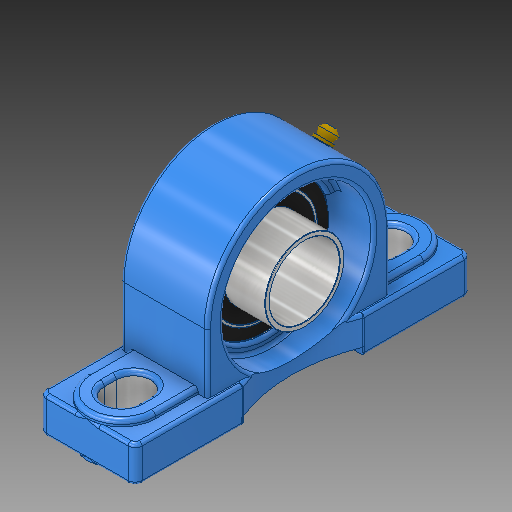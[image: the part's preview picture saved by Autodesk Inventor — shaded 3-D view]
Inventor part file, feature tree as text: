
AUTODESK INVENTOR PART (.ipt)
format: ipt  version: 2019 (Build 230136000, 136)  size: 796,672 bytes
history: native  units: mm
features: sketch x28, extrude x23, fillet x14, plane x8, mirror x6, revolve x1
ambient origin geometry x8: Origin, YZ Plane, XZ Plane, XY Plane, X Axis, Y Axis, Z Axis, Center Point
bodies: Solid1 (feature_tree)
feature tree (80):
  extrude  "Extrusion1"  Depth=167.0mm
  fillet  "Fillet1"  Radius=23.8mm
  plane  "Work Plane1"
  extrude  "Extrusion2"  Depth=18.0mm TaperAngle=0.0deg
  sketch  "Sketch3"  dims[d6=3.5mm d10=43.0mm d11=0.0mm]
  extrude  "Extrusion3"  Depth=43.0mm TaperAngle=0.0deg
  sketch  "Sketch4"  dims[d14=3.0mm d15=0.0mm d18=3.0mm d19=0.0mm]
  extrude  "Extrusion4"  Depth=3.0mm TaperAngle=0.0deg
  plane  "Work Plane2"
  mirror  "Mirror1"
  extrude  "Extrusion5"  Depth=74.25mm
  sketch  "Sketch7"  dims[d29=65.0mm d30=18.0mm d31=0.0mm]
  extrude  "Extrusion6"  Depth=18.0mm TaperAngle=0.0deg
  extrude  "Extrusion7"  Depth=18.0mm TaperAngle=0.0deg
  extrude  "Extrusion8"  Depth=1.58mm
  extrude  "Extrusion9"  Depth=1.58mm
  plane  "Work Plane4"
  mirror  "Mirror3"
  fillet  "Fillet2"  Radius=1.58mm
  fillet  "Fillet3"  Radius=1.58mm
  fillet  "Fillet4"  Radius=1.58mm
  fillet  "Fillet5"  [1 undecoded]
  plane  "Work Plane5"
  mirror  "Mirror4"
  fillet  "Fillet6"  Radius=65.0mm
  fillet  "Fillet7"  Radius=54.0mm
  plane  "Work Plane6"
  revolve  "Revolution1"  [1 undecoded]
  sketch  "Sketch14"  dims[d73=12.8mm d74=0.0mm d75=12.8mm d76=0.0mm]
  sketch  "Sketch15"  dims[d77=0.2mm d78=0.2mm]
  plane  "Work Plane7"
  extrude  "Extrusion10"  Depth=52.0mm
  plane  "Work Plane8"
  extrude  "Extrusion11"  Depth=12.8mm TaperAngle=0.0deg
  extrude  "Extrusion12"  Depth=0.2mm
  extrude  "Extrusion13"  Depth=42.9mm TaperAngle=0.0deg
  fillet  "Fillet8"  Radius=0.2mm
  fillet  "Fillet9"  Radius=0.2mm
  fillet  "Fillet10"  Radius=4.0mm
  extrude  "Extrusion14"  Depth=18.0mm TaperAngle=0.0deg
  fillet  "Fillet11"  Radius=63.5mm
  fillet  "Fillet12"  Radius=3.0mm
  extrude  "Extrusion15"  Depth=18.0mm TaperAngle=0.0deg
  sketch  "Sketch23"  dims[d105=3.0mm d106=17.0mm]
  sketch  "Sketch24"  dims[d107=21.0mm d108=0.0mm d109=2.0mm]
  extrude  "Extrusion16"  Depth=3.0mm TaperAngle=0.0deg
  sketch  "Sketch25"
  extrude  "Extrusion17"  Depth=2.0mm TaperAngle=0.0deg
  sketch  "Sketch26"
  extrude  "Extrusion18"  Depth=18.0mm
  extrude  "Extrusion19"  Depth=17.0mm
  extrude  "Extrusion20"  Depth=2.0mm
  fillet  "Fillet13"  [1 undecoded]
  plane  "Work Plane9"
  extrude  "Extrusion21"  [1 undecoded]
  extrude  "Extrusion22"  [1 undecoded]
  mirror  "Mirror5"
  mirror  "Mirror6"
  mirror  "Mirror7"
  extrude  "Extrusion23"  [1 undecoded]
  fillet  "Fillet14"  [1 undecoded]
  sketch  "Sketch1"  dims[d0=47.6mm d1=167.0mm d2=23.8mm]
  sketch  "Sketch2"  dims[d3=83.5mm d4=18.0mm d5=0.0mm]
  sketch  "Sketch5"  dims[d20=17.78mm d21=0.0mm d22=74.25mm]
  sketch  "Sketch6"  dims[d23=12.7mm d24=0.0mm d27=18.0mm d28=0.0mm]
  sketch  "Sketch8"  dims[d34=8.0mm d35=0.0mm d36=1.58mm]
  sketch  "Sketch9"  dims[d37=1.58mm d38=1.58mm d39=1.58mm d40=1.58mm d41=1.58mm d56=90.0deg]
  sketch  "Sketch10"  dims[d62=24.5mm d63=18.4mm d64=0.0mm d65=0.0mm d66=65.0mm d67=54.0mm]
  sketch  "Sketch11"  dims[d68=52.0mm d69=13.0mm d70=0.0mm]
  sketch  "Sketch13"  dims[d71=54.0mm d72=52.0mm]
  sketch  "Sketch17"  dims[d79=0.2mm d80=42.9mm d81=0.0mm d82=0.2mm d83=0.2mm d84=4.0mm d85=0.0mm]
  sketch  "Sketch18"  dims[d86=100.0mm d87=0.0mm d88=18.0mm d89=0.0mm d90=63.5mm d91=3.0mm]
  sketch  "Sketch19"  dims[d92=17.0mm d93=18.0mm d94=0.0mm]
  sketch  "Sketch20"  dims[d95=3.0mm d96=0.0mm d97=565.0mm d98=0.0mm]
  sketch  "Sketch21"  dims[d99=2.0mm d100=565.0mm d101=0.0mm]
  sketch  "Sketch22"  dims[d102=18.0mm d103=0.0mm d104=63.5mm]
  sketch  "Sketch27"
  sketch  "Sketch28"
  sketch  "Sketch29"
  sketch  "Sketch30"
note: 7 required parameter values undecoded (feature->parameter linkage not recoverable at this tier; creation-order binding heuristic only, values carry confidence <= 0.55)